# Revit family: kapelli-classik-gladkaya-belaya
name_source: partatom
category: Двери
revit_build: Autodesk Revit 2017 (Build: 20160225_1515(x64)
units: mm (PartAtom-declared; Revit-internal decimal feet)

## family parameters
Всегда вертикально = Да
Заголовок OmniClass = Doors
Номер OmniClass = 23.30.10.00
Общий = Нет
Основа = Стена
При загрузке вырезать с полостями = Нет
Точка расчета площади = Нет

## types (8) — shared parameters
Аналитическая конструкция = <Нет>
Водопоглащение (%) = 0.213
Замыкание стены = По основе
Звукоизоляция (дБ) = 33.3
Коробка.Глубина = 80 мм
Коробка.Ширина = 30 мм
Наличник двери = АС_Двери_Панели_KAPELLI
Обозначение = KAPELLI classic Гладкая белая
Описание = KAPELLI classic Гладкая белая
Полотно двери = АС_Двери_Панели_KAPELLI
Полотно.Высота = 2000 мм
Полотно.Толщина = 38 мм
Примерная высота = 2030 мм
Рама двери = АС_Двери_Панели_KAPELLI
Рама двери.Ширина вверху = 50 мм
Рама двери.Ширина внизу = 50 мм
Рама двери.Ширина слева = 50 мм
Рама двери.Ширина справа = 50 мм
Ручка двери = АС_Металл_KAPELLI
Сопротивление теплопередаче = 1.1510 (м²·K)/Вт
Тип конструкций = Дверь композитная
Тип полотна двери = АС_АР_Дверь_Панель_Полотно : Глухое
Толщина = 38 мм
Функция = Наружные слои

## per-type parameters (varying)
| type | Вес в сборе (кг) | Левая | Наименование | Полотно.Ширина | Правая | Примерная ширина |
| 600х2000 левая | 18.3 | Да | ДГ 21-7Л | 600 мм | Нет | 660 мм |
| 600х2000 | 18.3 | Нет | ДГ 21-7 | 600 мм | Да | 660 мм |
| 700х2000 левая | 19.5 | Да | ДГ 21-8Л | 700 мм | Нет | 760 мм |
| 700х2000 | 19.5 | Нет | ДГ 21-8 | 700 мм | Да | 760 мм |
| 800х2000 левая | 20.7 | Да | ДГ 21-9Л | 800 мм | Нет | 860 мм |
| 800х2000 | 20.7 | Нет | ДГ 21-9 | 800 мм | Да | 860 мм |
| 900х2000 левая | 21.9 | Да | ДГ 21-10Л | 900 мм | Нет | 960 мм |
| 900х2000 | 21.9 | Нет | ДГ 21-10 | 900 мм | Да | 960 мм |

## geometry (parser evidence)
native form markers: Blend x4, Sweep x6
no freeform markers — native parametric forms only
